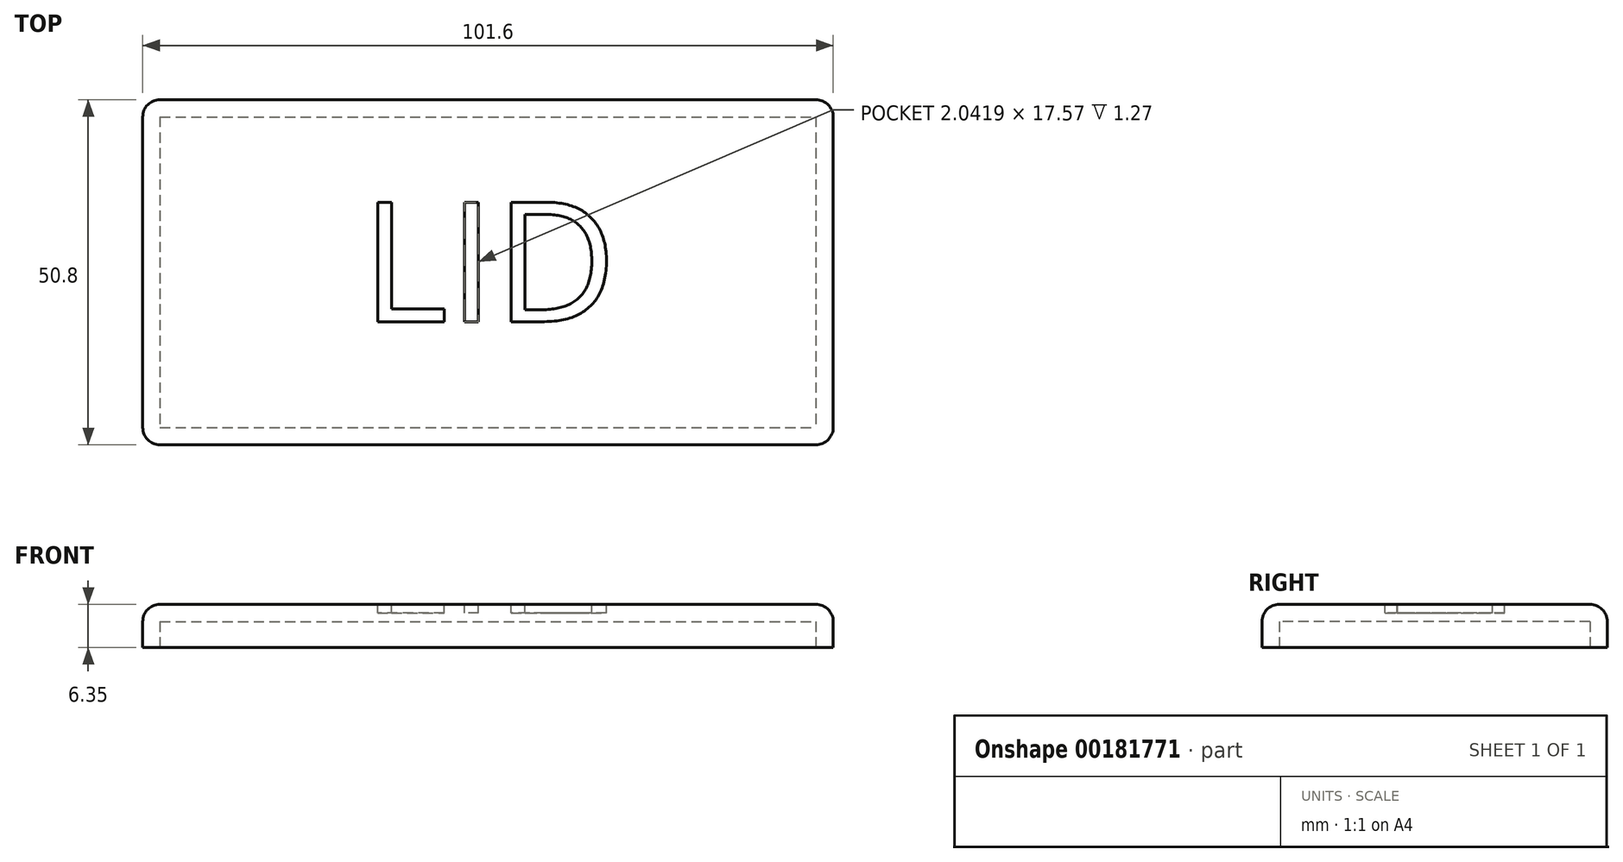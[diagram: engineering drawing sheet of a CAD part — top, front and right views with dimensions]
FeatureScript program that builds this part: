
annotation { "Feature Type Name" : "Feature", "Feature Type Description" : "" }
export const myFeature = defineFeature(function(context is Context, id is Id, definition is map)
    precondition{}
    {
        {
            var Q0;
            Q0=qCreatedBy(makeId("Top.planeOp"),FACE);
            var sketch = newSketch(context, id + "F0", { "sketchPlane" : qUnion([Q0])});
            skLineSegment(sketch, "E0.bottom", {"start": v(-69.82, 26.4) * mm, "end": v(31.78, 26.4) * mm});
            skLineSegment(sketch, "E0.top", {"start": v(-69.82, -24.4) * mm, "end": v(31.78, -24.4) * mm});
            skLineSegment(sketch, "E0.left", {"start": v(-69.82, 26.4) * mm, "end": v(-69.82, -24.4) * mm});
            skLineSegment(sketch, "E0.right", {"start": v(31.78, 26.4) * mm, "end": v(31.78, -24.4) * mm});
            skSolve(sketch);
        }
        {
            var Q0;
            Q0=makeQuery(id+"F0.imprint","IMPRINT",FACE,{"disambiguationData":[TD([[makeQuery(id+"F0.imprint","IMPRINT",EDGE,{"derivedFrom":sQuery(id+"F0.wireOp",EDGE,"E0.bottom")}),-1.0]])]});
            extrude(context, id + "F1", {"entities" : qUnion([Q0]), "depth" : 6.35 * mm});
        }
        {
            var Q0;
            Q0=makeQuery(id+"F1.opExtrude","CAP_FACE",FACE,{"disambiguationData":[OSD([sQuery(id+"F0.wireOp",EDGE,"E0.bottom"),sQuery(id+"F0.wireOp",EDGE,"E0.top"),sQuery(id+"F0.wireOp",EDGE,"E0.left"),sQuery(id+"F0.wireOp",EDGE,"E0.right")])],"isStart":true});
            shell(context, id + "F2", {"entities" : qUnion([Q0]), "thickness" : 2.54 * mm});
        }
        {
            var Q0;
            Q0=makeQuery(id+"F1.opExtrude","CAP_FACE",FACE,{"disambiguationData":[OSD([sQuery(id+"F0.wireOp",EDGE,"E0.bottom"),sQuery(id+"F0.wireOp",EDGE,"E0.top"),sQuery(id+"F0.wireOp",EDGE,"E0.left"),sQuery(id+"F0.wireOp",EDGE,"E0.right")])],"isStart":false});
            var Q1;
            Q1=makeQuery(id+"F1.opExtrude","SWEPT_EDGE",EDGE,{"disambiguationData":[OSD([sQuery(id+"F0.wireOp",EDGE,"E0.top"),sQuery(id+"F0.wireOp",EDGE,"E0.left")])]});
            var Q2;
            Q2=makeQuery(id+"F1.opExtrude","SWEPT_EDGE",EDGE,{"disambiguationData":[OSD([sQuery(id+"F0.wireOp",EDGE,"E0.top"),sQuery(id+"F0.wireOp",EDGE,"E0.right")])]});
            var Q3;
            Q3=makeQuery(id+"F1.opExtrude","SWEPT_EDGE",EDGE,{"disambiguationData":[OSD([sQuery(id+"F0.wireOp",EDGE,"E0.bottom"),sQuery(id+"F0.wireOp",EDGE,"E0.right")])]});
            var Q4;
            Q4=makeQuery(id+"F1.opExtrude","SWEPT_EDGE",EDGE,{"disambiguationData":[OSD([sQuery(id+"F0.wireOp",EDGE,"E0.bottom"),sQuery(id+"F0.wireOp",EDGE,"E0.left")])]});
            fillet(context, id + "F3", {"entities" : qUnion([Q0, Q1, Q2, Q3, Q4]), "radius" : 2.54 * mm, "tangentPropagation" : true, "allowEdgeOverflow" : false});
        }
        {
            var Q0;
            Q0=makeQuery(id+"F1.opExtrude","CAP_FACE",FACE,{"disambiguationData":[OSD([sQuery(id+"F0.wireOp",EDGE,"E0.bottom"),sQuery(id+"F0.wireOp",EDGE,"E0.top"),sQuery(id+"F0.wireOp",EDGE,"E0.left"),sQuery(id+"F0.wireOp",EDGE,"E0.right")])],"isStart":false});
            var sketch = newSketch(context, id + "F4", { "sketchPlane" : qUnion([Q0])});
            skText(sketch, "E1", { "text": "LID", "fontName": "OpenSans-Regular.ttf"});
            const initialGuessF4  = {"E1": [-0.03766, -0.00629, 1, 0, 0.01772]};
            skSetInitialGuess(sketch, initialGuessF4);
            skSolve(sketch);
        }
        {
            var Q0;
            Q0 = qSketchRegion(id + "F4", true);
            extrude(context, id + "F5", {"entities" : qUnion([Q0]), "operationType" : NewBodyOperationType.REMOVE, "oppositeDirection" : true, "depth" : 1.27 * mm});
        }
    });
